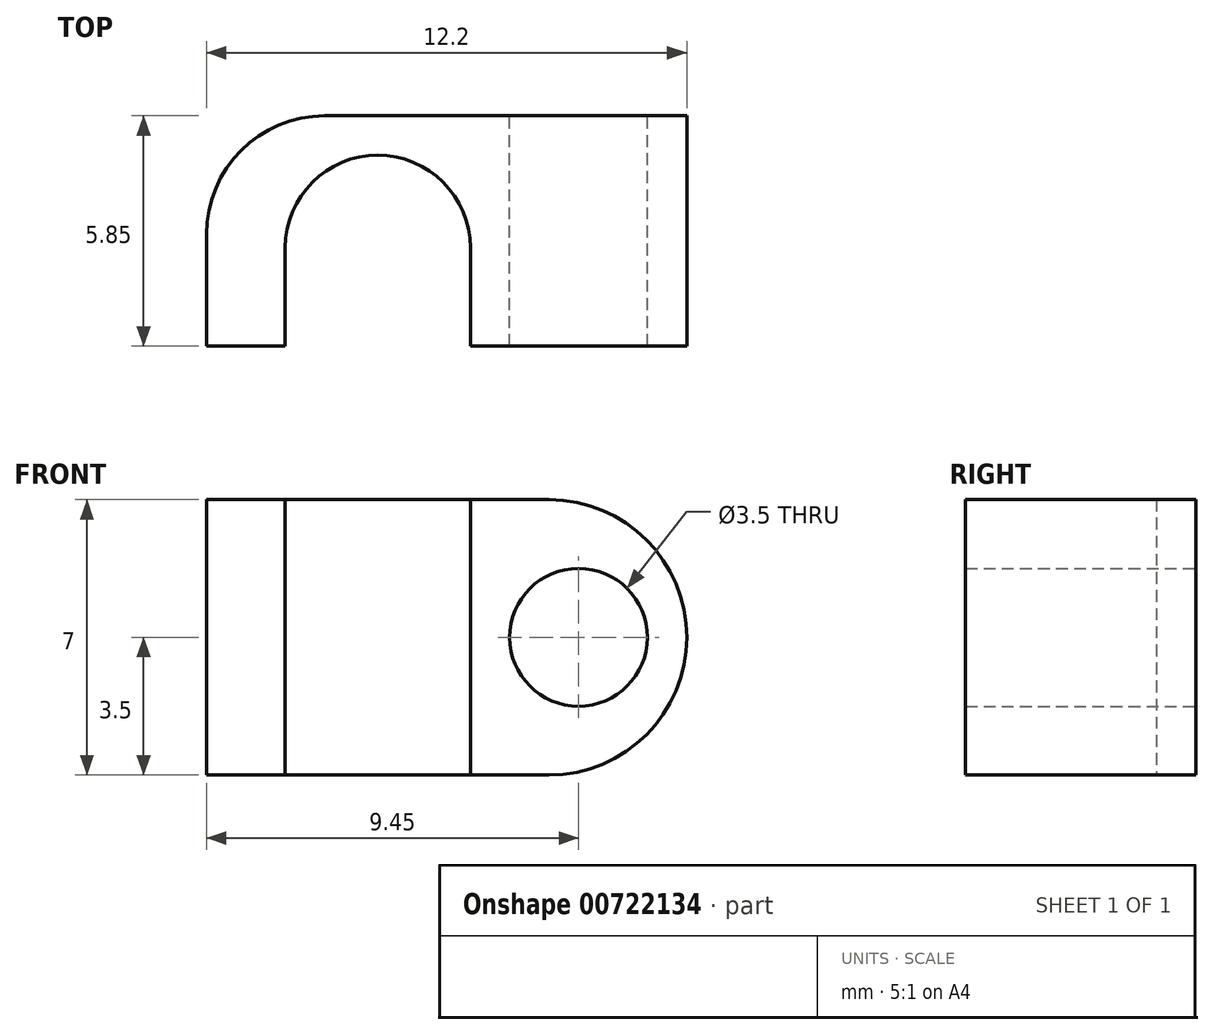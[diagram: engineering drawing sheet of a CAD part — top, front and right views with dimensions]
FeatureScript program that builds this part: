
annotation { "Feature Type Name" : "Feature", "Feature Type Description" : "" }
export const myFeature = defineFeature(function(context is Context, id is Id, definition is map)
    precondition{}
    {
        {
            var Q0;
            Q0=qCreatedBy(makeId("Top.planeOp"),FACE);
            var sketch = newSketch(context, id + "F0", { "sketchPlane" : qUnion([Q0])});
            skArc(sketch, "E0", {"start": v(2.35, 0) * mm, "mid": v(0, 2.35) * mm, "end": v(-2.35, 0) * mm});
            skLineSegment(sketch, "E1.left", {"start": v(-2.35, 0) * mm, "end": v(-2.35, -2.5) * mm});
            skLineSegment(sketch, "E1.right", {"start": v(2.35, 0) * mm, "end": v(2.35, -2.5) * mm});
            skPoint(sketch, "E2.firstSnap0", {"position": v(0, -2.5) * mm});
            skLineSegment(sketch, "E2.bottom", {"start": v(-4.35, -2.5) * mm, "end": v(-2.35, -2.5) * mm});
            skLineSegment(sketch, "E2.top", {"start": v(-4.35, 3.35) * mm, "end": v(7.85, 3.35) * mm});
            skLineSegment(sketch, "E2.left", {"start": v(-4.35, -2.5) * mm, "end": v(-4.35, 3.35) * mm});
            skLineSegment(sketch, "E2.right", {"start": v(7.85, -2.5) * mm, "end": v(7.85, 3.35) * mm});
            skLineSegment(sketch, "E3.trimOffspring", {"start": v(2.35, -2.5) * mm, "end": v(7.85, -2.5) * mm});
            skSolve(sketch);
        }
        {
            var Q0;
            Q0=makeQuery(id+"F0.imprint","IMPRINT",FACE,{"disambiguationData":[TD([[makeQuery(id+"F0.imprint","IMPRINT",EDGE,{"derivedFrom":sQuery(id+"F0.wireOp",EDGE,"E0")}),-1.0]])]});
            extrude(context, id + "F1", {"entities" : qUnion([Q0]), "depth" : 7 * mm, "offsetDistance" : 25 * mm});
        }
        {
            var Q0;
            Q0=makeQuery(id+"F1.opExtrude","SWEPT_FACE",FACE,{"disambiguationData":[OSD([sQuery(id+"F0.wireOp",EDGE,"E2.top")])]});
            var sketch = newSketch(context, id + "F2", { "sketchPlane" : qUnion([Q0])});
            skLineSegment(sketch, "E4.0", {"start": v(-2.35, 0) * mm, "end": v(-7.85, 0) * mm, "construction": true});
            skLineSegment(sketch, "E5.0", {"start": v(-7.85, 7) * mm, "end": v(-7.85, 0) * mm, "construction": true});
            skLineSegment(sketch, "E5.1", {"start": v(-2.35, 7) * mm, "end": v(-7.85, 7) * mm, "construction": true});
            skLineSegment(sketch, "E6", {"start": v(-2.35, 0) * mm, "end": v(-7.85, 7) * mm, "construction": true});
            skLineSegment(sketch, "E7", {"start": v(-7.85, 0) * mm, "end": v(-2.35, 7) * mm, "construction": true});
            skPoint(sketch, "E8", {"position": v(-5.1, 3.5) * mm});
            skCircle(sketch, "E9", {"center": v(-5.1, 3.5) * mm, "radius": 1.75 * mm});
            skSolve(sketch);
        }
        {
            var Q0;
            Q0=makeQuery(id+"F2.imprint","IMPRINT",FACE,{"disambiguationData":[TD([[makeQuery(id+"F2.imprint","IMPRINT",EDGE,{"derivedFrom":sQuery(id+"F2.wireOp",EDGE,"E9")}),1.0]])]});
            var Q1;
            Q1=sQuery(id+"F2.wireOp",EDGE,"E9");
            var Q2;
            Q2=makeQuery(id+"F1.opExtrude","SWEPT_FACE",FACE,{"disambiguationData":[OSD([sQuery(id+"F0.wireOp",EDGE,"E3.trimOffspring")])]});
            extrude(context, id + "F3", {"entities" : qUnion([Q0]), "operationType" : NewBodyOperationType.REMOVE, "surfaceEntities" : qUnion([Q1]), "endBound" : BoundingType.UP_TO_SURFACE, "oppositeDirection" : true, "depth" : 25 * mm, "endBoundEntityFace" : qUnion([Q2]), "offsetDistance" : 25 * mm});
        }
        {
            var Q0;
            Q0=makeQuery(id+"F1.opExtrude","CAP_EDGE",EDGE,{"disambiguationData":[OSD([sQuery(id+"F0.wireOp",EDGE,"E2.right")])],"isStart":false});
            var Q1;
            Q1=makeQuery(id+"F1.opExtrude","CAP_EDGE",EDGE,{"disambiguationData":[OSD([sQuery(id+"F0.wireOp",EDGE,"E2.right")])],"isStart":true});
            fillet(context, id + "F4", {"entities" : qUnion([Q0, Q1]), "radius" : 3.5 * mm, "tangentPropagation" : true, "allowEdgeOverflow" : false});
        }
        {
            var Q0;
            Q0=makeQuery(id+"F1.opExtrude","SWEPT_EDGE",EDGE,{"disambiguationData":[OSD([sQuery(id+"F0.wireOp",EDGE,"E2.top"),sQuery(id+"F0.wireOp",EDGE,"E2.left")])]});
            fillet(context, id + "F5", {"entities" : qUnion([Q0]), "radius" : 3 * mm, "tangentPropagation" : true, "allowEdgeOverflow" : false});
        }
    });
